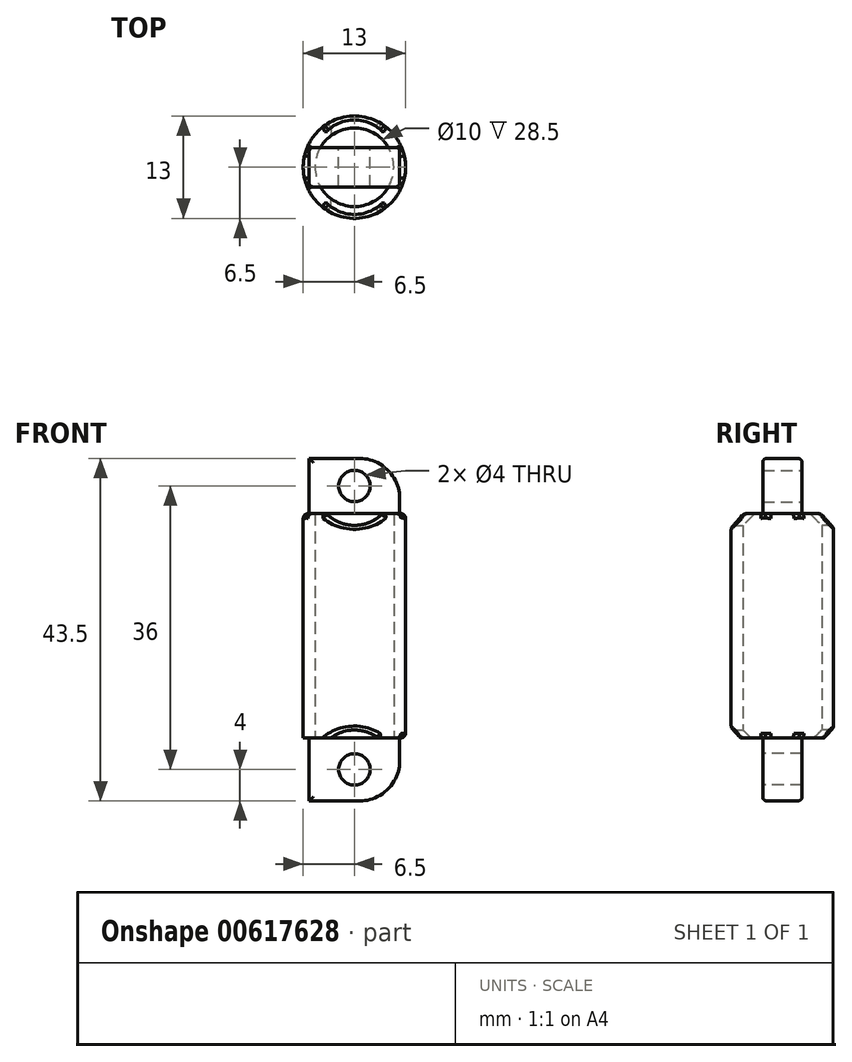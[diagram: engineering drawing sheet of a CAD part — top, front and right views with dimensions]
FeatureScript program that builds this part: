
annotation { "Feature Type Name" : "Feature", "Feature Type Description" : "" }
export const myFeature = defineFeature(function(context is Context, id is Id, definition is map)
    precondition{}
    {
        {
            var Q0;
            Q0=qCreatedBy(makeId("Top.planeOp"),FACE);
            var sketch = newSketch(context, id + "F0", { "sketchPlane" : qUnion([Q0])});
            skCircle(sketch, "E0", {"center": v(0, 0) * mm, "radius": 6.5 * mm});
            skSolve(sketch);
        }
        {
            var Q0;
            Q0 = qSketchRegion(id + "F0", true);
            extrude(context, id + "F1", {"entities" : qUnion([Q0]), "depth" : 28.5 * mm, "offsetDistance" : 25 * mm});
        }
        {
            var Q0;
            Q0=qCreatedBy(makeId("Top.planeOp"),FACE);
            var sketch = newSketch(context, id + "F2", { "sketchPlane" : qUnion([Q0])});
            skLineSegment(sketch, "E1.bottom", {"start": v(5.75, 2.5) * mm, "end": v(-5.75, 2.5) * mm});
            skLineSegment(sketch, "E1.top", {"start": v(5.75, -2.5) * mm, "end": v(-5.75, -2.5) * mm});
            skLineSegment(sketch, "E1.left", {"start": v(5.75, 2.5) * mm, "end": v(5.75, -2.5) * mm});
            skLineSegment(sketch, "E1.right", {"start": v(-5.75, 2.5) * mm, "end": v(-5.75, -2.5) * mm});
            skPoint(sketch, "E1.middle", {"position": v(0, 0) * mm});
            skSolve(sketch);
        }
        {
            var Q0;
            Q0=makeQuery(id+"F1.opExtrude","CAP_FACE",FACE,{"disambiguationData":[OSD([sQuery(id+"F0.wireOp",EDGE,"E0")])],"isStart":false});
            var Q1;
            Q1=makeQuery(id+"F1.opExtrude","CAP_FACE",FACE,{"disambiguationData":[OSD([sQuery(id+"F0.wireOp",EDGE,"E0")])],"isStart":true});
            shell(context, id + "F3", {"entities" : qUnion([Q0, Q1]), "thickness" : 1.5 * mm});
        }
        {
            var Q0;
            Q0 = qSketchRegion(id + "F2", true);
            extrude(context, id + "F4", {"entities" : qUnion([Q0]), "operationType" : NewBodyOperationType.ADD, "oppositeDirection" : true, "depth" : 8 * mm, "offsetDistance" : 25 * mm});
        }
        {
            var Q0;
            Q0=makeQuery(id+"F1.opExtrude","CAP_FACE",FACE,{"disambiguationData":[OSD([sQuery(id+"F0.wireOp",EDGE,"E0")])],"isStart":false});
            var sketch = newSketch(context, id + "F5", { "sketchPlane" : qUnion([Q0])});
            skLineSegment(sketch, "E2.bottom", {"start": v(5.75, 2.5) * mm, "end": v(-5.75, 2.5) * mm});
            skLineSegment(sketch, "E2.top", {"start": v(5.75, -2.5) * mm, "end": v(-5.75, -2.5) * mm});
            skLineSegment(sketch, "E2.left", {"start": v(5.75, 2.5) * mm, "end": v(5.75, -2.5) * mm});
            skLineSegment(sketch, "E2.right", {"start": v(-5.75, 2.5) * mm, "end": v(-5.75, -2.5) * mm});
            skPoint(sketch, "E2.middle", {"position": v(0, 0) * mm});
            skSolve(sketch);
        }
        {
            var Q0;
            Q0 = qSketchRegion(id + "F5", true);
            extrude(context, id + "F6", {"entities" : qUnion([Q0]), "operationType" : NewBodyOperationType.ADD, "depth" : 7 * mm, "offsetDistance" : 25 * mm});
        }
        {
            var Q0;
            Q0=makeQuery(id+"F6.opExtrude","SWEPT_FACE",FACE,{"disambiguationData":[OSD([sQuery(id+"F5.wireOp",EDGE,"E2.bottom")])]});
            var sketch = newSketch(context, id + "F7", { "sketchPlane" : qUnion([Q0])});
            skCircle(sketch, "E3", {"center": v(0, 32) * mm, "radius": 2 * mm});
            skPoint(sketch, "E3.centerSnap0", {"position": v(-5.75, 32) * mm});
            skSolve(sketch);
        }
        {
            var Q0;
            Q0 = qSketchRegion(id + "F7", true);
            extrude(context, id + "F8", {"entities" : qUnion([Q0]), "operationType" : NewBodyOperationType.REMOVE, "oppositeDirection" : true, "depth" : 5 * mm, "offsetDistance" : 25 * mm});
        }
        {
            var Q0;
            Q0=makeQuery(id+"F4.opExtrude","SWEPT_FACE",FACE,{"disambiguationData":[OSD([sQuery(id+"F2.wireOp",EDGE,"E1.top")])]});
            var sketch = newSketch(context, id + "F9", { "sketchPlane" : qUnion([Q0])});
            skCircle(sketch, "E4", {"center": v(0, -4) * mm, "radius": 2 * mm});
            skPoint(sketch, "E4.centerSnap0", {"position": v(-5.75, -4) * mm});
            skSolve(sketch);
        }
        {
            var Q0;
            Q0 = qSketchRegion(id + "F9", true);
            extrude(context, id + "F10", {"entities" : qUnion([Q0]), "operationType" : NewBodyOperationType.REMOVE, "oppositeDirection" : true, "depth" : 5 * mm, "offsetDistance" : 25 * mm});
        }
        {
            var Q0;
            Q0=makeQuery(id+"F4.opExtrude","CAP_EDGE",EDGE,{"disambiguationData":[OSD([sQuery(id+"F2.wireOp",EDGE,"E1.left")])],"isStart":false});
            var Q1;
            Q1=makeQuery(id+"F6.opExtrude","CAP_EDGE",EDGE,{"disambiguationData":[OSD([sQuery(id+"F5.wireOp",EDGE,"E2.left")])],"isStart":false});
            fillet(context, id + "F11", {"entities" : qUnion([Q0, Q1]), "radius" : 5 * mm, "tangentPropagation" : true, "rho" : 0.4, "crossSection" : FilletCrossSection.CONIC, "allowEdgeOverflow" : false});
        }
        {
            var Q0;
            Q0=makeQuery(id+"F6.opExtrude","SWEPT_EDGE",EDGE,{"disambiguationData":[OSD([sQuery(id+"F5.wireOp",EDGE,"E2.top"),sQuery(id+"F5.wireOp",EDGE,"E2.right")])]});
            var Q1;
            Q1=makeQuery(id+"F6.opExtrude","SWEPT_EDGE",EDGE,{"disambiguationData":[OSD([sQuery(id+"F5.wireOp",EDGE,"E2.bottom"),sQuery(id+"F5.wireOp",EDGE,"E2.right")])]});
            var Q2;
            Q2=makeQuery(id+"F11.opFillet","BLEND_EDGE",EDGE,{"blendedFrom":[makeQuery(id+"F6.opExtrude","CAP_EDGE",EDGE,{"disambiguationData":[OSD([sQuery(id+"F5.wireOp",EDGE,"E2.left")])],"isStart":false}),makeQuery(id+"F6.opExtrude","SWEPT_FACE",FACE,{"disambiguationData":[OSD([sQuery(id+"F5.wireOp",EDGE,"E2.bottom")])]})],"blendedInto":[makeQuery(id+"F6.opExtrude","SWEPT_FACE",FACE,{"disambiguationData":[OSD([sQuery(id+"F5.wireOp",EDGE,"E2.bottom")])]})]});
            var Q3;
            Q3=makeQuery(id+"F11.opFillet","BLEND_EDGE",EDGE,{"blendedFrom":[makeQuery(id+"F6.opExtrude","CAP_EDGE",EDGE,{"disambiguationData":[OSD([sQuery(id+"F5.wireOp",EDGE,"E2.left")])],"isStart":false}),makeQuery(id+"F6.opExtrude","SWEPT_FACE",FACE,{"disambiguationData":[OSD([sQuery(id+"F5.wireOp",EDGE,"E2.top")])]})],"blendedInto":[makeQuery(id+"F6.opExtrude","SWEPT_FACE",FACE,{"disambiguationData":[OSD([sQuery(id+"F5.wireOp",EDGE,"E2.top")])]})]});
            var Q4;
            Q4=makeQuery(id+"F4.opExtrude","SWEPT_EDGE",EDGE,{"disambiguationData":[OSD([sQuery(id+"F2.wireOp",EDGE,"E1.top"),sQuery(id+"F2.wireOp",EDGE,"E1.right")])]});
            var Q5;
            Q5=makeQuery(id+"F4.opExtrude","SWEPT_EDGE",EDGE,{"disambiguationData":[OSD([sQuery(id+"F2.wireOp",EDGE,"E1.bottom"),sQuery(id+"F2.wireOp",EDGE,"E1.right")])]});
            var Q6;
            Q6=makeQuery(id+"F4.opExtrude","CAP_EDGE",EDGE,{"disambiguationData":[OSD([sQuery(id+"F2.wireOp",EDGE,"E1.top")])],"isStart":false});
            var Q7;
            Q7=makeQuery(id+"F11.opFillet","BLEND_EDGE",EDGE,{"blendedFrom":[makeQuery(id+"F4.opExtrude","CAP_EDGE",EDGE,{"disambiguationData":[OSD([sQuery(id+"F2.wireOp",EDGE,"E1.left")])],"isStart":false}),makeQuery(id+"F4.opExtrude","SWEPT_FACE",FACE,{"disambiguationData":[OSD([sQuery(id+"F2.wireOp",EDGE,"E1.bottom")])]})],"blendedInto":[makeQuery(id+"F4.opExtrude","SWEPT_FACE",FACE,{"disambiguationData":[OSD([sQuery(id+"F2.wireOp",EDGE,"E1.bottom")])]})]});
            fillet(context, id + "F12", {"entities" : qUnion([Q0, Q1, Q2, Q3, Q4, Q5, Q6, Q7]), "radius" : 0.5 * mm, "tangentPropagation" : true, "allowEdgeOverflow" : false});
        }
        {
            var Q0;
            Q0=makeQuery(id+"F6.opExtrude","SWEPT_FACE",FACE,{"disambiguationData":[OSD([sQuery(id+"F5.wireOp",EDGE,"E2.top")])]});
            var sketch = newSketch(context, id + "F13", { "sketchPlane" : qUnion([Q0])});
            skCircle(sketch, "E5", {"center": v(0, 32) * mm, "radius": 5 * mm});
            skSolve(sketch);
        }
        {
            var Q0;
            Q0 = qSketchRegion(id + "F13", true);
            extrude(context, id + "F14", {"entities" : qUnion([Q0]), "operationType" : NewBodyOperationType.REMOVE, "depth" : 5 * mm, "offsetDistance" : 25 * mm});
        }
        {
            var Q0;
            Q0=makeQuery(id+"F6.opExtrude","SWEPT_FACE",FACE,{"disambiguationData":[OSD([sQuery(id+"F5.wireOp",EDGE,"E2.bottom")])]});
            var sketch = newSketch(context, id + "F15", { "sketchPlane" : qUnion([Q0])});
            skCircle(sketch, "E6", {"center": v(0, 32) * mm, "radius": 5 * mm});
            skSolve(sketch);
        }
        {
            var Q0;
            Q0 = qSketchRegion(id + "F15", true);
            extrude(context, id + "F16", {"entities" : qUnion([Q0]), "operationType" : NewBodyOperationType.REMOVE, "depth" : 5 * mm, "offsetDistance" : 25 * mm});
        }
        {
            var Q0;
            Q0=makeQuery(id+"F4.opExtrude","SWEPT_FACE",FACE,{"disambiguationData":[OSD([sQuery(id+"F2.wireOp",EDGE,"E1.top")])]});
            var sketch = newSketch(context, id + "F17", { "sketchPlane" : qUnion([Q0])});
            skCircle(sketch, "E7", {"center": v(0, -4) * mm, "radius": 5 * mm});
            skSolve(sketch);
        }
        {
            var Q0;
            Q0 = qSketchRegion(id + "F17", true);
            extrude(context, id + "F18", {"entities" : qUnion([Q0]), "operationType" : NewBodyOperationType.REMOVE, "depth" : 5 * mm, "offsetDistance" : 25 * mm});
        }
        {
            var Q0;
            Q0=makeQuery(id+"F4.opExtrude","SWEPT_FACE",FACE,{"disambiguationData":[OSD([sQuery(id+"F2.wireOp",EDGE,"E1.bottom")])]});
            var sketch = newSketch(context, id + "F19", { "sketchPlane" : qUnion([Q0])});
            skCircle(sketch, "E8", {"center": v(0, -4) * mm, "radius": 5 * mm});
            skSolve(sketch);
        }
        {
            var Q0;
            Q0 = qSketchRegion(id + "F19", true);
            extrude(context, id + "F20", {"entities" : qUnion([Q0]), "operationType" : NewBodyOperationType.REMOVE, "depth" : 5 * mm, "offsetDistance" : 25 * mm});
        }
        {
            var Q0;
            Q0=makeQuery(id+"F16.boolean.opBoolean","SPLIT",EDGE,{"disambiguationData":[OD(0.0)],"derivedFrom":makeQuery(id+"F1.opExtrude","CAP_EDGE",EDGE,{"disambiguationData":[OSD([sQuery(id+"F0.wireOp",EDGE,"E0")])],"isStart":false})});
            var Q1;
            Q1=makeQuery(id+"F16.boolean.opBoolean","SPLIT",EDGE,{"disambiguationData":[OD(1.0)],"derivedFrom":makeQuery(id+"F1.opExtrude","CAP_EDGE",EDGE,{"disambiguationData":[OSD([sQuery(id+"F0.wireOp",EDGE,"E0")])],"isStart":false})});
            var Q2;
            Q2=makeQuery(id+"F20.boolean.opBoolean","SPLIT",EDGE,{"disambiguationData":[OD(0.0)],"derivedFrom":makeQuery(id+"F1.opExtrude","CAP_EDGE",EDGE,{"disambiguationData":[OSD([sQuery(id+"F0.wireOp",EDGE,"E0")])],"isStart":true})});
            fillet(context, id + "F21", {"entities" : qUnion([Q0, Q1, Q2]), "radius" : 0.6 * mm, "tangentPropagation" : true, "allowEdgeOverflow" : false});
        }
        {
            var Q0;
            Q0=makeQuery(id+"F20.boolean.opBoolean","INTERSECT",EDGE,{"derivedFrom":[makeQuery(id+"F1.opExtrude","SWEPT_FACE",FACE,{"disambiguationData":[OSD([sQuery(id+"F0.wireOp",EDGE,"E0")])]}),makeQuery(id+"F20.opExtrude","SWEPT_FACE",FACE,{"disambiguationData":[OSD([sQuery(id+"F19.wireOp",EDGE,"E8")])]})]});
            var Q1;
            Q1=makeQuery(id+"F16.boolean.opBoolean","INTERSECT",EDGE,{"derivedFrom":[makeQuery(id+"F1.opExtrude","SWEPT_FACE",FACE,{"disambiguationData":[OSD([sQuery(id+"F0.wireOp",EDGE,"E0")])]}),makeQuery(id+"F16.opExtrude","SWEPT_FACE",FACE,{"disambiguationData":[OSD([sQuery(id+"F15.wireOp",EDGE,"E6")])]})]});
            var Q2;
            Q2=makeQuery(id+"F14.boolean.opBoolean","INTERSECT",EDGE,{"derivedFrom":[makeQuery(id+"F1.opExtrude","SWEPT_FACE",FACE,{"disambiguationData":[OSD([sQuery(id+"F0.wireOp",EDGE,"E0")])]}),makeQuery(id+"F14.opExtrude","SWEPT_FACE",FACE,{"disambiguationData":[OSD([sQuery(id+"F13.wireOp",EDGE,"E5")])]})]});
            var Q3;
            Q3=makeQuery(id+"F18.boolean.opBoolean","INTERSECT",EDGE,{"derivedFrom":[makeQuery(id+"F1.opExtrude","SWEPT_FACE",FACE,{"disambiguationData":[OSD([sQuery(id+"F0.wireOp",EDGE,"E0")])]}),makeQuery(id+"F18.opExtrude","SWEPT_FACE",FACE,{"disambiguationData":[OSD([sQuery(id+"F17.wireOp",EDGE,"E7")])]})]});
            fillet(context, id + "F22", {"entities" : qUnion([Q0, Q1, Q2, Q3]), "radius" : 0.5 * mm, "tangentPropagation" : true, "allowEdgeOverflow" : false});
        }
    });
